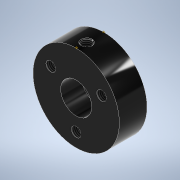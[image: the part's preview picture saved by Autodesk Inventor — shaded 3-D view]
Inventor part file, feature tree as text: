
AUTODESK INVENTOR PART (.ipt)
format: ipt  version: 2022 (Build 260153000, 153)  size: 177,152 bytes
history: native  units: mm
features: other x5, thread x4, extrude x3, sketch x2, plane x2, chamfer x1, projected_geometry x1
ambient origin geometry x8: Origin, YZ Plane, XZ Plane, XY Plane, X Axis, Y Axis, Z Axis, Center Point
bodies: Solid1 (feature_tree)
feature tree (18):
  sketch  "Sketch1"  dims[d0=25.0mm d1=17.0mm]
  extrude  "Extrusion1"  Depth=17.0mm
  extrude  "Extrusion2"  Depth=8.0mm
  other  "Work Axis1"
  other  "Work Axis2"
  plane  "Work Plane2"
  extrude  "Extrusion3"  Depth=2.8mm
  chamfer  "Chamfer1"  Distance=30.0mm Angle=360.0deg
  thread  "Thread1"  [1 undecoded]
  thread  "Thread2"  [1 undecoded]
  thread  "Thread3"  [1 undecoded]
  thread  "Thread4"  [1 undecoded]
  plane  "Work Plane1"
  other  "Work Point1"
  other  "Work Point2"
  other  "Work Axis3"
  sketch  "Sketch2"  dims[d2=9.0mm d3=8.0mm d4=2.8mm d5=30.0mm d7=360.0deg d9=8.0mm d10=0.0mm d11=6.0mm d12=0.0mm d13=90.0deg d14=2.8mm d16=6.0mm d17=0.0mm d18=0.2mm d19=2.0mm d20=45.0deg d21=5.0mm d22=8.0mm d23=0.0mm d24=8.0mm d25=0.0mm d26=8.0mm d27=0.0mm d28=8.046mm d29=0.0mm]
  projected_geometry  "Projected Loop1"
note: 4 required parameter values undecoded (feature->parameter linkage not recoverable at this tier; creation-order binding heuristic only, values carry confidence <= 0.55)
